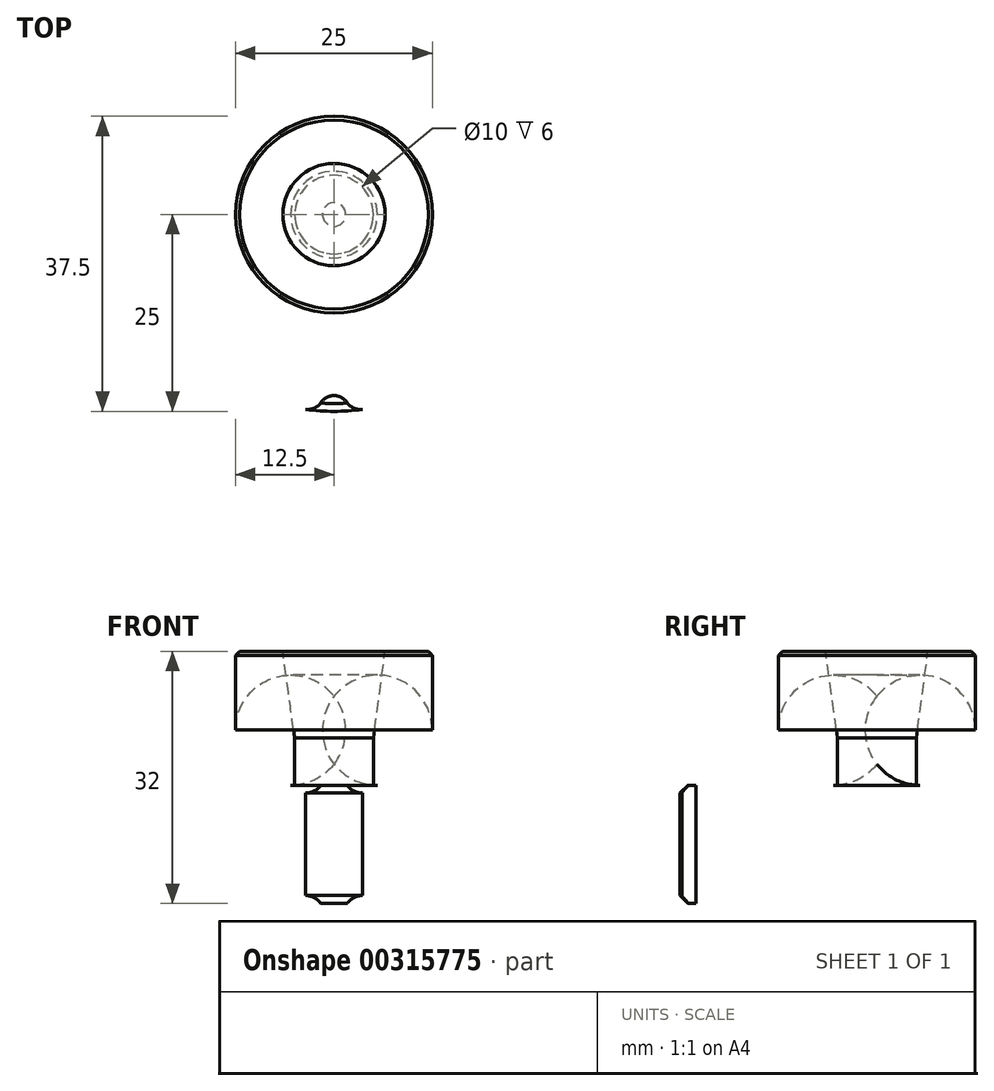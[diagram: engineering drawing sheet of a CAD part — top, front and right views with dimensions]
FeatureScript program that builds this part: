
annotation { "Feature Type Name" : "Feature", "Feature Type Description" : "" }
export const myFeature = defineFeature(function(context is Context, id is Id, definition is map)
    precondition{}
    {
        {
            var Q0;
            Q0=qCreatedBy(makeId("Top.planeOp"),FACE);
            var sketch = newSketch(context, id + "F0", { "sketchPlane" : qUnion([Q0])});
            skCircle(sketch, "E0", {"center": v(0, 0) * mm, "radius": 25 * mm});
            skSolve(sketch);
        }
        {
            var Q0;
            Q0=makeQuery(id+"F0.imprint","IMPRINT",FACE,{"disambiguationData":[TD([[makeQuery(id+"F0.imprint","IMPRINT",EDGE,{"derivedFrom":sQuery(id+"F0.wireOp",EDGE,"E0")}),1.0]])]});
            extrude(context, id + "F1", {"entities" : qUnion([Q0]), "depth" : 15 * mm});
        }
        {
            var Q0;
            Q0=makeQuery(id+"F1.opExtrude","CAP_FACE",FACE,{"disambiguationData":[OSD([sQuery(id+"F0.wireOp",EDGE,"E0")])],"isStart":true});
            var sketch = newSketch(context, id + "F2", { "sketchPlane" : qUnion([Q0])});
            skCircle(sketch, "E1", {"center": v(0, 0) * mm, "radius": 23 * mm, "construction": true});
            skArc(sketch, "E2", {"start": v(0, 23) * mm, "mid": v(-0.94, 23.23) * mm, "end": v(-1.66, 23.88) * mm});
            skPoint(sketch, "E3.visualSharp", {"position": v(-2, 24.92) * mm});
            skArc(sketch, "E3.filletArc", {"start": v(-1.66, 23.88) * mm, "mid": v(-2.5, 24.59) * mm, "end": v(-3.6, 24.74) * mm});
            skCircle(sketch, "E4", {"center": v(0, 0) * mm, "radius": 25 * mm, "construction": true});
            skArc(sketch, "E5.MirrorCS", {"start": v(1.66, 23.88) * mm, "mid": v(2.5, 24.59) * mm, "end": v(3.6, 24.74) * mm});
            skArc(sketch, "E6.MirrorCS", {"start": v(0, 23) * mm, "mid": v(0.94, 23.23) * mm, "end": v(1.66, 23.88) * mm});
            skArc(sketch, "E7.1.0", {"start": v(-15.38, 18.35) * mm, "mid": v(-16.48, 18.42) * mm, "end": v(-17.46, 17.9) * mm});
            skArc(sketch, "E7.1.1", {"start": v(-13.52, 18.6) * mm, "mid": v(-14.42, 18.25) * mm, "end": v(-15.38, 18.35) * mm});
            skArc(sketch, "E7.1.2", {"start": v(-13.52, 18.6) * mm, "mid": v(-12.9, 19.35) * mm, "end": v(-12.7, 20.3) * mm});
            skArc(sketch, "E7.1.3", {"start": v(-12.7, 20.3) * mm, "mid": v(-12.43, 21.37) * mm, "end": v(-11.63, 22.13) * mm});
            skArc(sketch, "E7.2.0", {"start": v(-23.22, 5.8) * mm, "mid": v(-24.16, 5.22) * mm, "end": v(-24.64, 4.22) * mm});
            skArc(sketch, "E7.2.1", {"start": v(-21.87, 7.1) * mm, "mid": v(-22.39, 6.29) * mm, "end": v(-23.22, 5.8) * mm});
            skArc(sketch, "E7.2.2", {"start": v(-21.87, 7.1) * mm, "mid": v(-21.8, 8.07) * mm, "end": v(-22.2, 8.96) * mm});
            skArc(sketch, "E7.2.3", {"start": v(-22.2, 8.96) * mm, "mid": v(-22.61, 9.98) * mm, "end": v(-22.42, 11.07) * mm});
            skArc(sketch, "E7.3.0", {"start": v(-22.2, -8.96) * mm, "mid": v(-22.61, -9.98) * mm, "end": v(-22.42, -11.07) * mm});
            skArc(sketch, "E7.3.1", {"start": v(-21.87, -7.1) * mm, "mid": v(-21.8, -8.07) * mm, "end": v(-22.2, -8.96) * mm});
            skArc(sketch, "E7.3.2", {"start": v(-21.87, -7.1) * mm, "mid": v(-22.39, -6.29) * mm, "end": v(-23.22, -5.8) * mm});
            skArc(sketch, "E7.3.3", {"start": v(-23.22, -5.8) * mm, "mid": v(-24.16, -5.22) * mm, "end": v(-24.64, -4.22) * mm});
            skArc(sketch, "E7.4.0", {"start": v(-12.7, -20.3) * mm, "mid": v(-12.43, -21.37) * mm, "end": v(-11.63, -22.13) * mm});
            skArc(sketch, "E7.4.1", {"start": v(-13.52, -18.6) * mm, "mid": v(-12.9, -19.35) * mm, "end": v(-12.7, -20.3) * mm});
            skArc(sketch, "E7.4.2", {"start": v(-13.52, -18.6) * mm, "mid": v(-14.42, -18.25) * mm, "end": v(-15.38, -18.35) * mm});
            skArc(sketch, "E7.4.3", {"start": v(-15.38, -18.35) * mm, "mid": v(-16.48, -18.42) * mm, "end": v(-17.46, -17.9) * mm});
            skArc(sketch, "E7.5.0", {"start": v(1.66, -23.88) * mm, "mid": v(2.5, -24.59) * mm, "end": v(3.6, -24.74) * mm});
            skArc(sketch, "E7.5.1", {"start": v(0, -23) * mm, "mid": v(0.94, -23.23) * mm, "end": v(1.66, -23.88) * mm});
            skArc(sketch, "E7.5.2", {"start": v(0, -23) * mm, "mid": v(-0.94, -23.23) * mm, "end": v(-1.66, -23.88) * mm});
            skArc(sketch, "E7.5.3", {"start": v(-1.66, -23.88) * mm, "mid": v(-2.5, -24.59) * mm, "end": v(-3.6, -24.74) * mm});
            skArc(sketch, "E7.6.0", {"start": v(15.38, -18.35) * mm, "mid": v(16.48, -18.42) * mm, "end": v(17.46, -17.9) * mm});
            skArc(sketch, "E7.6.1", {"start": v(13.52, -18.6) * mm, "mid": v(14.42, -18.25) * mm, "end": v(15.38, -18.35) * mm});
            skArc(sketch, "E7.6.2", {"start": v(13.52, -18.6) * mm, "mid": v(12.9, -19.35) * mm, "end": v(12.7, -20.3) * mm});
            skArc(sketch, "E7.6.3", {"start": v(12.7, -20.3) * mm, "mid": v(12.43, -21.37) * mm, "end": v(11.63, -22.13) * mm});
            skArc(sketch, "E7.7.0", {"start": v(23.22, -5.8) * mm, "mid": v(24.16, -5.22) * mm, "end": v(24.64, -4.22) * mm});
            skArc(sketch, "E7.7.1", {"start": v(21.87, -7.1) * mm, "mid": v(22.39, -6.29) * mm, "end": v(23.22, -5.8) * mm});
            skArc(sketch, "E7.7.2", {"start": v(21.87, -7.1) * mm, "mid": v(21.8, -8.07) * mm, "end": v(22.2, -8.96) * mm});
            skArc(sketch, "E7.7.3", {"start": v(22.2, -8.96) * mm, "mid": v(22.61, -9.98) * mm, "end": v(22.42, -11.07) * mm});
            skArc(sketch, "E7.8.0", {"start": v(22.2, 8.96) * mm, "mid": v(22.61, 9.98) * mm, "end": v(22.42, 11.07) * mm});
            skArc(sketch, "E7.8.1", {"start": v(21.87, 7.1) * mm, "mid": v(21.8, 8.07) * mm, "end": v(22.2, 8.96) * mm});
            skArc(sketch, "E7.8.2", {"start": v(21.87, 7.1) * mm, "mid": v(22.39, 6.29) * mm, "end": v(23.22, 5.8) * mm});
            skArc(sketch, "E7.8.3", {"start": v(23.22, 5.8) * mm, "mid": v(24.16, 5.22) * mm, "end": v(24.64, 4.22) * mm});
            skArc(sketch, "E7.9.0", {"start": v(12.7, 20.3) * mm, "mid": v(12.43, 21.37) * mm, "end": v(11.63, 22.13) * mm});
            skArc(sketch, "E7.9.1", {"start": v(13.52, 18.6) * mm, "mid": v(12.9, 19.35) * mm, "end": v(12.7, 20.3) * mm});
            skArc(sketch, "E7.9.2", {"start": v(13.52, 18.6) * mm, "mid": v(14.42, 18.25) * mm, "end": v(15.38, 18.35) * mm});
            skArc(sketch, "E7.9.3", {"start": v(15.38, 18.35) * mm, "mid": v(16.48, 18.42) * mm, "end": v(17.46, 17.9) * mm});
            skSolve(sketch);
        }
        {
            var Q0;
            {var subQ1=sQuery(id+"F2.wireOp",EDGE,"E7.1.0");Q0=makeQuery(id+"F2.imprint","IMPRINT",FACE,{"disambiguationData":[TD([[makeQuery(id+"F2.imprint","IMPRINT",EDGE,{"derivedFrom":subQ1}),-1.0]])]});}
            var Q1;
            Q1=makeQuery(id+"F2.imprint","IMPRINT",FACE,{"disambiguationData":[TD([[makeQuery(id+"F2.imprint","IMPRINT",EDGE,{"derivedFrom":sQuery(id+"F2.wireOp",EDGE,"E2")}),-1.0]])]});
            var Q2;
            {var subQ1=sQuery(id+"F2.wireOp",EDGE,"E7.9.0");Q2=makeQuery(id+"F2.imprint","IMPRINT",FACE,{"disambiguationData":[TD([[makeQuery(id+"F2.imprint","IMPRINT",EDGE,{"derivedFrom":subQ1}),-1.0]])]});}
            var Q3;
            {var subQ1=sQuery(id+"F2.wireOp",EDGE,"E7.8.0");Q3=makeQuery(id+"F2.imprint","IMPRINT",FACE,{"disambiguationData":[TD([[makeQuery(id+"F2.imprint","IMPRINT",EDGE,{"derivedFrom":subQ1}),-1.0]])]});}
            var Q4;
            {var subQ1=sQuery(id+"F2.wireOp",EDGE,"E7.7.0");Q4=makeQuery(id+"F2.imprint","IMPRINT",FACE,{"disambiguationData":[TD([[makeQuery(id+"F2.imprint","IMPRINT",EDGE,{"derivedFrom":subQ1}),-1.0]])]});}
            var Q5;
            {var subQ1=sQuery(id+"F2.wireOp",EDGE,"E7.6.0");Q5=makeQuery(id+"F2.imprint","IMPRINT",FACE,{"disambiguationData":[TD([[makeQuery(id+"F2.imprint","IMPRINT",EDGE,{"derivedFrom":subQ1}),-1.0]])]});}
            var Q6;
            {var subQ1=sQuery(id+"F2.wireOp",EDGE,"E7.5.0");Q6=makeQuery(id+"F2.imprint","IMPRINT",FACE,{"disambiguationData":[TD([[makeQuery(id+"F2.imprint","IMPRINT",EDGE,{"derivedFrom":subQ1}),-1.0]])]});}
            var Q7;
            {var subQ1=sQuery(id+"F2.wireOp",EDGE,"E7.4.0");Q7=makeQuery(id+"F2.imprint","IMPRINT",FACE,{"disambiguationData":[TD([[makeQuery(id+"F2.imprint","IMPRINT",EDGE,{"derivedFrom":subQ1}),-1.0]])]});}
            var Q8;
            {var subQ1=sQuery(id+"F2.wireOp",EDGE,"E7.3.0");Q8=makeQuery(id+"F2.imprint","IMPRINT",FACE,{"disambiguationData":[TD([[makeQuery(id+"F2.imprint","IMPRINT",EDGE,{"derivedFrom":subQ1}),-1.0]])]});}
            var Q9;
            {var subQ1=sQuery(id+"F2.wireOp",EDGE,"E7.2.0");Q9=makeQuery(id+"F2.imprint","IMPRINT",FACE,{"disambiguationData":[TD([[makeQuery(id+"F2.imprint","IMPRINT",EDGE,{"derivedFrom":subQ1}),-1.0]])]});}
            extrude(context, id + "F3", {"entities" : qUnion([Q0, Q1, Q2, Q3, Q4, Q5, Q6, Q7, Q8, Q9]), "operationType" : NewBodyOperationType.REMOVE, "oppositeDirection" : true, "depth" : 25 * mm});
        }
        {
            var Q0;
            Q0=makeQuery(id+"F1.opExtrude","CAP_FACE",FACE,{"disambiguationData":[OSD([sQuery(id+"F0.wireOp",EDGE,"E0")])],"isStart":false});
            var sketch = newSketch(context, id + "F4", { "sketchPlane" : qUnion([Q0])});
            skCircle(sketch, "E8", {"center": v(0, 0) * mm, "radius": 12.5 * mm});
            skSolve(sketch);
        }
        {
            var Q0;
            Q0=makeQuery(id+"F4.imprint","IMPRINT",FACE,{"disambiguationData":[TD([[makeQuery(id+"F4.imprint","IMPRINT",EDGE,{"derivedFrom":sQuery(id+"F4.wireOp",EDGE,"E8")}),1.0]])]});
            extrude(context, id + "F5", {"entities" : qUnion([Q0]), "operationType" : NewBodyOperationType.ADD, "depth" : 17 * mm});
        }
        {
            var Q0;
            Q0=makeQuery(id+"F5.opExtrude","CAP_FACE",FACE,{"disambiguationData":[OSD([sQuery(id+"F4.wireOp",EDGE,"E8")])],"isStart":false});
            var sketch = newSketch(context, id + "F6", { "sketchPlane" : qUnion([Q0])});
            skPoint(sketch, "E9", {"position": v(0, 0) * mm});
            skSolve(sketch);
        }
        {
            var Q0;
            Q0=qCreatedBy(makeId("Right.planeOp"),FACE);
            var sketch = newSketch(context, id + "F7", { "sketchPlane" : qUnion([Q0])});
            skLineSegment(sketch, "E10", {"start": v(0, 32) * mm, "end": v(0, 12) * mm});
            skLineSegment(sketch, "E11", {"start": v(0, 12) * mm, "end": v(5, 12) * mm});
            skLineSegment(sketch, "E12", {"start": v(5, 12) * mm, "end": v(5, 21) * mm});
            skPoint(sketch, "E13.orphan", {"position": v(12.5, 32) * mm});
            skPoint(sketch, "E14.orphan", {"position": v(-12.5, 32) * mm});
            skLineSegment(sketch, "E15", {"start": v(5, 21) * mm, "end": v(6.5, 32) * mm});
            skLineSegment(sketch, "E16", {"start": v(0, 32) * mm, "end": v(6.5, 32) * mm});
            skSolve(sketch);
        }
        {
            var Q0;
            Q0 = qSketchRegion(id + "F7", true);
            var Q1;
            Q1=sQuery(id+"F7.wireOp",EDGE,"E10");
            revolve(context, id + "F8", {"operationType" : NewBodyOperationType.REMOVE, "entities" : qUnion([Q0]), "axis" : qUnion([Q1]), "revolveType" : RevolveType.FULL, "oppositeDirection" : true});
        }
        {
            var Q0;
            Q0=makeQuery(id+"F1.opExtrude","CAP_FACE",FACE,{"disambiguationData":[OSD([sQuery(id+"F0.wireOp",EDGE,"E0")])],"isStart":true});
            var sketch = newSketch(context, id + "F9", { "sketchPlane" : qUnion([Q0])});
            skPoint(sketch, "E17", {"position": v(0, 0) * mm});
            skSolve(sketch);
        }
        {
            var Q0;
            Q0=sQuery(id+"F9.wireOp",VERTEX,"E17");
            var Q1;
            Q1=makeQuery(id+"F1.opExtrude","SWEPT_BODY",BODY,{"disambiguationData":[OSD([sQuery(id+"F0.wireOp",EDGE,"E0")])]});
            hole(context, id + "F10", {"style" : HoleStyle.C_BORE, "endStyle" : HoleEndStyle.THROUGH, "holeDiameter" : 5.5 * mm, "cBoreDiameter" : 9 * mm, "cBoreDepth" : 7 * mm, "tappedDepth" : 12 * mm, "tapClearance" : 3, "locations" : qUnion([Q0]), "scope" : qUnion([Q1])});
        }
        {
            var Q0;
            Q0=makeQuery(id+"F5.opExtrude","CAP_EDGE",EDGE,{"disambiguationData":[OSD([sQuery(id+"F4.wireOp",EDGE,"E8")])],"isStart":true});
            fillet(context, id + "F11", {"entities" : qUnion([Q0]), "radius" : 7 * mm, "tangentPropagation" : true, "allowEdgeOverflow" : false});
        }
        {
            var Q0;
            Q0=makeQuery(id+"F10.hole-0.boolean.opBoolean","COPY",EDGE,{"derivedFrom":makeQuery(id+"F10.hole-0.opRevolve","SWEPT_EDGE",EDGE,{"disambiguationData":[OSD([sQuery(id+"F10.hole-0.sketch.wireOp",EDGE,"cbore_start_line_2"),sQuery(id+"F10.hole-0.sketch.wireOp",EDGE,"cbore_start_line_3")])]})});
            var Q1;
            Q1=makeQuery(id+"F5.opExtrude","CAP_EDGE",EDGE,{"disambiguationData":[OSD([sQuery(id+"F4.wireOp",EDGE,"E8")])],"isStart":false});
            var Q2;
            Q2=makeQuery(id+"FMbtTcFD1xUZaOf_1.opChamfer","BLEND_EDGE",EDGE,{"blendedFrom":[makeQuery(id+"Fod8D2pc0eP7lrV_1.hole-0.boolean.opBoolean","COPY",EDGE,{"derivedFrom":makeQuery(id+"Fod8D2pc0eP7lrV_1.hole-0.opRevolve","SWEPT_EDGE",EDGE,{"disambiguationData":[OSD([sQuery(id+"Fod8D2pc0eP7lrV_1.hole-0.sketch.wireOp",EDGE,"core_line_2"),sQuery(id+"Fod8D2pc0eP7lrV_1.hole-0.sketch.wireOp",EDGE,"core_line_3")])]})}),makeQuery(id+"F5.opExtrude","CAP_FACE",FACE,{"disambiguationData":[OSD([sQuery(id+"F4.wireOp",EDGE,"E8")])],"isStart":false})],"blendedInto":[makeQuery(id+"F5.opExtrude","CAP_FACE",FACE,{"disambiguationData":[OSD([sQuery(id+"F4.wireOp",EDGE,"E8")])],"isStart":false})]});
            var Q3;
            Q3=makeQuery(id+"F8.boolean.opBoolean","COPY",EDGE,{"derivedFrom":makeQuery(id+"F8.opRevolve","SWEPT_EDGE",EDGE,{"disambiguationData":[OSD([sQuery(id+"F7.wireOp",EDGE,"E15"),sQuery(id+"F7.wireOp",EDGE,"E16")])]})});
            chamfer(context, id + "F12", {"entities" : qUnion([Q0, Q1, Q2, Q3]), "width" : 0.5 * mm, "tangentPropagation" : true});
        }
        {
            var Q0;
            Q0=makeQuery(id+"F1.opExtrude","CAP_EDGE",EDGE,{"disambiguationData":[OSD([sQuery(id+"F0.wireOp",EDGE,"E0")])],"isStart":true});
            var Q1;
            Q1=makeQuery(id+"F1.opExtrude","CAP_EDGE",EDGE,{"disambiguationData":[OSD([sQuery(id+"F0.wireOp",EDGE,"E0")])],"isStart":false});
            chamfer(context, id + "F13", {"entities" : qUnion([Q0, Q1]), "width" : 1 * mm, "tangentPropagation" : true});
        }
    });
